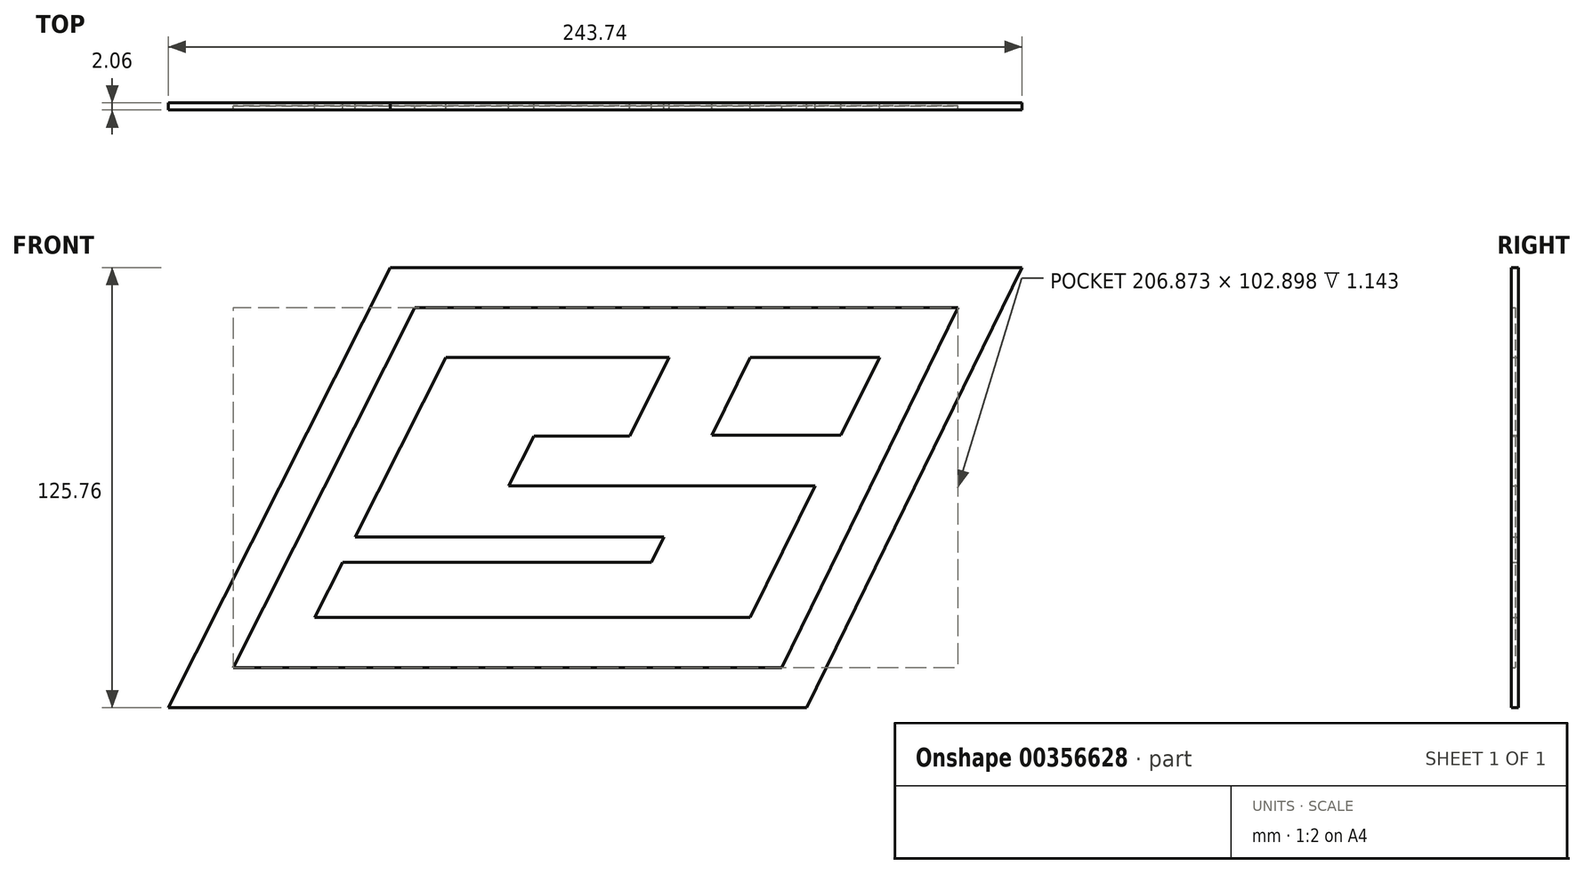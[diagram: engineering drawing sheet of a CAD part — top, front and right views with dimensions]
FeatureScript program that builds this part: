
annotation { "Feature Type Name" : "Feature", "Feature Type Description" : "" }
export const myFeature = defineFeature(function(context is Context, id is Id, definition is map)
    precondition{}
    {
        {
            var Q0;
            Q0=qCreatedBy(makeId("Front.planeOp"),FACE);
            var sketch = newSketch(context, id + "F0", { "sketchPlane" : qUnion([Q0])});
            skLineSegment(sketch, "E0", {"start": v(-12.43, 33) * mm, "end": v(15.1, 33) * mm, "construction": true});
            skLineSegment(sketch, "E1", {"start": v(15.1, 33) * mm, "end": v(6.9, 16.48) * mm, "construction": true});
            skLineSegment(sketch, "E2", {"start": v(6.9, 16.48) * mm, "end": v(-20.75, 16.48) * mm, "construction": true});
            skLineSegment(sketch, "E3", {"start": v(-20.75, 16.48) * mm, "end": v(-12.43, 33) * mm, "construction": true});
            skLineSegment(sketch, "E4", {"start": v(-12.43, 33) * mm, "end": v(1.74, 33) * mm});
            skLineSegment(sketch, "E5", {"start": v(1.74, 33) * mm, "end": v(-0.77, 28.01) * mm});
            skLineSegment(sketch, "E6", {"start": v(-0.77, 28.01) * mm, "end": v(-6.84, 28.01) * mm});
            skLineSegment(sketch, "E7", {"start": v(-6.84, 28.01) * mm, "end": v(-8.43, 24.86) * mm});
            skLineSegment(sketch, "E8", {"start": v(-8.43, 24.86) * mm, "end": v(11, 24.86) * mm});
            skPoint(sketch, "E8.endSnap0", {"position": v(11, 24.74) * mm});
            skLineSegment(sketch, "E9", {"start": v(11, 24.86) * mm, "end": v(6.9, 16.48) * mm});
            skLineSegment(sketch, "E10", {"start": v(-20.75, 16.48) * mm, "end": v(-18.97, 20) * mm});
            skLineSegment(sketch, "E11", {"start": v(-18.97, 20) * mm, "end": v(0.6, 20) * mm});
            skLineSegment(sketch, "E12", {"start": v(0.6, 20) * mm, "end": v(1.4, 21.6) * mm});
            skLineSegment(sketch, "E13", {"start": v(1.4, 21.6) * mm, "end": v(-18.16, 21.6) * mm});
            skLineSegment(sketch, "E14", {"start": v(-18.16, 21.6) * mm, "end": v(-12.43, 33) * mm});
            skLineSegment(sketch, "E15", {"start": v(6.9, 33) * mm, "end": v(4.45, 28.06) * mm});
            skLineSegment(sketch, "E16", {"start": v(4.45, 28.06) * mm, "end": v(12.65, 28.06) * mm});
            skLineSegment(sketch, "E17", {"start": v(12.65, 28.06) * mm, "end": v(15.1, 33) * mm});
            skLineSegment(sketch, "E18", {"start": v(-20.75, 16.48) * mm, "end": v(6.9, 16.48) * mm});
            skLineSegment(sketch, "E19", {"start": v(6.9, 33) * mm, "end": v(15.1, 33) * mm});
            skSolve(sketch);
        }
        {
            var Q0;
            Q0=makeQuery(id+"F0.imprint","IMPRINT",FACE,{"disambiguationData":[TD([[makeQuery(id+"F0.imprint","IMPRINT",EDGE,{"derivedFrom":sQuery(id+"F0.wireOp",EDGE,"E4")}),-1.0]])]});
            var Q1;
            Q1=makeQuery(id+"F0.imprint","IMPRINT",FACE,{"disambiguationData":[TD([[makeQuery(id+"F0.imprint","IMPRINT",EDGE,{"derivedFrom":sQuery(id+"F0.wireOp",EDGE,"E15")}),1.0]])]});
            var Q2;
            Q2=qSketchRegion(id+"F2",true);
            extrude(context, id + "F1", {"entities" : qUnion([Q0, Q1, Q2]), "depth" : 0.4 * mm, "offsetDistance" : 25.4 * mm});
        }
        {
            var Q0;
            Q0=qCreatedBy(makeId("Front.planeOp"),FACE);
            var sketch = newSketch(context, id + "F2", { "sketchPlane" : qUnion([Q0])});
            skLineSegment(sketch, "E20", {"start": v(-25.9, 13.3) * mm, "end": v(8.88, 13.3) * mm});
            skLineSegment(sketch, "E21", {"start": v(8.88, 13.3) * mm, "end": v(20.07, 36.17) * mm});
            skLineSegment(sketch, "E22", {"start": v(20.07, 36.17) * mm, "end": v(-14.38, 36.17) * mm});
            skLineSegment(sketch, "E23", {"start": v(-14.38, 36.17) * mm, "end": v(-25.9, 13.3) * mm});
            skSolve(sketch);
        }
        {
            var Q0;
            Q0=makeQuery(id+"F2.imprint","IMPRINT",FACE,{"disambiguationData":[TD([[makeQuery(id+"F2.imprint","IMPRINT",EDGE,{"derivedFrom":sQuery(id+"F2.wireOp",EDGE,"E20")}),1.0]])]});
            extrude(context, id + "F3", {"entities" : qUnion([Q0]), "depth" : 0.2 * mm, "offsetDistance" : 25.4 * mm});
        }
        {
            var Q0;
            Q0=qCreatedBy(makeId("Front.planeOp"),FACE);
            var sketch = newSketch(context, id + "F4", { "sketchPlane" : qUnion([Q0])});
            skLineSegment(sketch, "E24", {"start": v(-30.02, 10.77) * mm, "end": v(-15.95, 38.71) * mm});
            skLineSegment(sketch, "E25", {"start": v(-15.95, 38.71) * mm, "end": v(24.14, 38.71) * mm});
            skLineSegment(sketch, "E26", {"start": v(24.14, 38.71) * mm, "end": v(10.47, 10.77) * mm});
            skLineSegment(sketch, "E27", {"start": v(10.47, 10.77) * mm, "end": v(-30.02, 10.77) * mm});
            skLineSegment(sketch, "E28", {"start": v(-14.38, 36.17) * mm, "end": v(20.07, 36.17) * mm});
            skLineSegment(sketch, "E29", {"start": v(20.07, 36.17) * mm, "end": v(8.88, 13.3) * mm});
            skLineSegment(sketch, "E30", {"start": v(8.88, 13.3) * mm, "end": v(-25.9, 13.3) * mm});
            skLineSegment(sketch, "E31", {"start": v(-25.9, 13.3) * mm, "end": v(-14.38, 36.17) * mm});
            skSolve(sketch);
        }
        {
            var Q0;
            Q0=makeQuery(id+"F4.imprint","IMPRINT",FACE,{"disambiguationData":[TD([[makeQuery(id+"F4.imprint","IMPRINT",EDGE,{"derivedFrom":sQuery(id+"F4.wireOp",EDGE,"E24")}),-1.0]])]});
            extrude(context, id + "F5", {"entities" : qUnion([Q0]), "operationType" : NewBodyOperationType.ADD, "depth" : 0.46 * mm, "offsetDistance" : 25.4 * mm});
        }
        {
            var Q0;
            Q0=makeQuery(id+"F3.opExtrude","SWEPT_BODY",BODY,{"disambiguationData":[OSD([sQuery(id+"F2.wireOp",EDGE,"E20"),sQuery(id+"F2.wireOp",EDGE,"E21"),sQuery(id+"F2.wireOp",EDGE,"E22"),sQuery(id+"F2.wireOp",EDGE,"E23")])]});
            var Q1;
            Q1=makeQuery(id+"F1.opExtrude","SWEPT_BODY",BODY,{"disambiguationData":[OSD([sQuery(id+"F0.wireOp",EDGE,"E15"),sQuery(id+"F0.wireOp",EDGE,"E16"),sQuery(id+"F0.wireOp",EDGE,"E17"),sQuery(id+"F0.wireOp",EDGE,"E19")])]});
            var Q2;
            Q2=makeQuery(id+"F1.opExtrude","SWEPT_BODY",BODY,{"disambiguationData":[OSD([sQuery(id+"F0.wireOp",EDGE,"E4"),sQuery(id+"F0.wireOp",EDGE,"E5"),sQuery(id+"F0.wireOp",EDGE,"E6"),sQuery(id+"F0.wireOp",EDGE,"E7"),sQuery(id+"F0.wireOp",EDGE,"E8"),sQuery(id+"F0.wireOp",EDGE,"E9"),sQuery(id+"F0.wireOp",EDGE,"E10"),sQuery(id+"F0.wireOp",EDGE,"E11"),sQuery(id+"F0.wireOp",EDGE,"E12"),sQuery(id+"F0.wireOp",EDGE,"E13"),sQuery(id+"F0.wireOp",EDGE,"E14"),sQuery(id+"F0.wireOp",EDGE,"E18")])]});
            var Q3;
            Q3=sQuery(id+"F0.wireOp",VERTEX,"E7.start");
            transform(context, id + "F6", {"entities" : qUnion([Q0, Q1, Q2]), "transformType" : TransformType.SCALE_UNIFORMLY, "scale" : 4.5, "scalePoint" : qUnion([Q3]), "makeCopy" : false});
        }
    });
